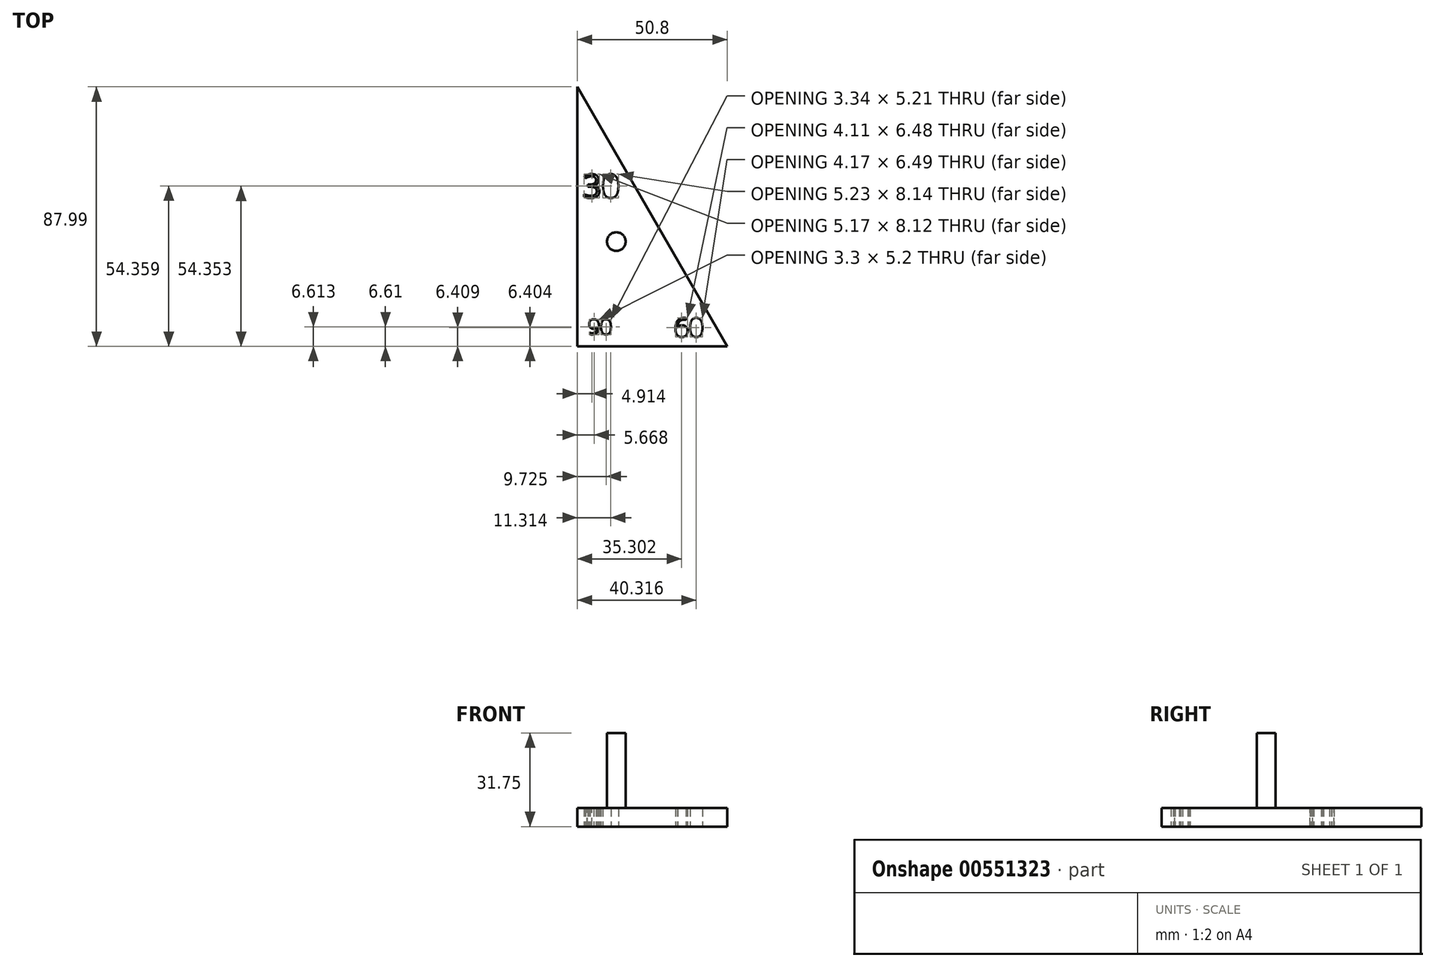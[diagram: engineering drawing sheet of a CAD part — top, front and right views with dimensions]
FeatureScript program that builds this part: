
annotation { "Feature Type Name" : "Feature", "Feature Type Description" : "" }
export const myFeature = defineFeature(function(context is Context, id is Id, definition is map)
    precondition{}
    {
        {
            var Q0;
            Q0=qCreatedBy(makeId("Top.planeOp"),FACE);
            var sketch = newSketch(context, id + "F0", { "sketchPlane" : qUnion([Q0])});
            skLineSegment(sketch, "E0", {"start": v(0, 0) * mm, "end": v(0, 87.99) * mm});
            skLineSegment(sketch, "E1", {"start": v(0, 87.99) * mm, "end": v(50.8, 0) * mm});
            skLineSegment(sketch, "E2", {"start": v(50.8, 0) * mm, "end": v(0, 0) * mm});
            skText(sketch, "E3", { "text": "90", "fontName": "OpenSans-Regular.ttf"});
            skText(sketch, "E4", { "text": "30", "fontName": "OpenSans-Regular.ttf"});
            skText(sketch, "E5", { "text": "60", "fontName": "OpenSans-Regular.ttf"});
            const initialGuessF0  = {"E3": [0.00365, 0.00408, 1, 0, 0.0051], "E4": [0.00182, 0.0504, 1, 0, 0.00797], "E5": [0.03274, 0.00325, 1, 0, 0.00636]};
            skSetInitialGuess(sketch, initialGuessF0);
            skSolve(sketch);
        }
        {
            var Q0;
            Q0 = qSketchRegion(id + "F0", true);
            extrude(context, id + "F1", {"entities" : qUnion([Q0]), "depth" : 6.35 * mm, "offsetDistance" : 25.4 * mm});
        }
        {
            var Q0;
            Q0=makeQuery(id+"F1.opExtrude","CAP_FACE",FACE,{"disambiguationData":[OSD([sQuery(id+"F0.wireOp",EDGE,"E0"),sQuery(id+"F0.wireOp",EDGE,"E1"),sQuery(id+"F0.wireOp",EDGE,"E2"),sQuery(id+"F0.wireOp",EDGE,"E3.sketch_text.stroke-0"),sQuery(id+"F0.wireOp",EDGE,"E3.sketch_text.stroke-1"),sQuery(id+"F0.wireOp",EDGE,"E3.sketch_text.stroke-2"),sQuery(id+"F0.wireOp",EDGE,"E3.sketch_text.stroke-3"),sQuery(id+"F0.wireOp",EDGE,"E3.sketch_text.stroke-4"),sQuery(id+"F0.wireOp",EDGE,"E3.sketch_text.stroke-5"),sQuery(id+"F0.wireOp",EDGE,"E3.sketch_text.stroke-6"),sQuery(id+"F0.wireOp",EDGE,"E3.sketch_text.stroke-7"),sQuery(id+"F0.wireOp",EDGE,"E3.sketch_text.stroke-8"),sQuery(id+"F0.wireOp",EDGE,"E3.sketch_text.stroke-9"),sQuery(id+"F0.wireOp",EDGE,"E3.sketch_text.stroke-10"),sQuery(id+"F0.wireOp",EDGE,"E3.sketch_text.stroke-11"),sQuery(id+"F0.wireOp",EDGE,"E3.sketch_text.stroke-12"),sQuery(id+"F0.wireOp",EDGE,"E3.sketch_text.stroke-13"),sQuery(id+"F0.wireOp",EDGE,"E3.sketch_text.stroke-14"),sQuery(id+"F0.wireOp",EDGE,"E3.sketch_text.stroke-15"),sQuery(id+"F0.wireOp",EDGE,"E3.sketch_text.stroke-26"),sQuery(id+"F0.wireOp",EDGE,"E3.sketch_text.stroke-27"),sQuery(id+"F0.wireOp",EDGE,"E3.sketch_text.stroke-28"),sQuery(id+"F0.wireOp",EDGE,"E3.sketch_text.stroke-29"),sQuery(id+"F0.wireOp",EDGE,"E3.sketch_text.stroke-30"),sQuery(id+"F0.wireOp",EDGE,"E3.sketch_text.stroke-31"),sQuery(id+"F0.wireOp",EDGE,"E3.sketch_text.stroke-32"),sQuery(id+"F0.wireOp",EDGE,"E3.sketch_text.stroke-33"),sQuery(id+"F0.wireOp",EDGE,"E4.sketch_text.stroke-0"),sQuery(id+"F0.wireOp",EDGE,"E4.sketch_text.stroke-1"),sQuery(id+"F0.wireOp",EDGE,"E4.sketch_text.stroke-2"),sQuery(id+"F0.wireOp",EDGE,"E4.sketch_text.stroke-3"),sQuery(id+"F0.wireOp",EDGE,"E4.sketch_text.stroke-4"),sQuery(id+"F0.wireOp",EDGE,"E4.sketch_text.stroke-5"),sQuery(id+"F0.wireOp",EDGE,"E4.sketch_text.stroke-6"),sQuery(id+"F0.wireOp",EDGE,"E4.sketch_text.stroke-7"),sQuery(id+"F0.wireOp",EDGE,"E4.sketch_text.stroke-8"),sQuery(id+"F0.wireOp",EDGE,"E4.sketch_text.stroke-9"),sQuery(id+"F0.wireOp",EDGE,"E4.sketch_text.stroke-10"),sQuery(id+"F0.wireOp",EDGE,"E4.sketch_text.stroke-11"),sQuery(id+"F0.wireOp",EDGE,"E4.sketch_text.stroke-12"),sQuery(id+"F0.wireOp",EDGE,"E4.sketch_text.stroke-13"),sQuery(id+"F0.wireOp",EDGE,"E4.sketch_text.stroke-14"),sQuery(id+"F0.wireOp",EDGE,"E4.sketch_text.stroke-15"),sQuery(id+"F0.wireOp",EDGE,"E4.sketch_text.stroke-16"),sQuery(id+"F0.wireOp",EDGE,"E4.sketch_text.stroke-17"),sQuery(id+"F0.wireOp",EDGE,"E4.sketch_text.stroke-18"),sQuery(id+"F0.wireOp",EDGE,"E4.sketch_text.stroke-19"),sQuery(id+"F0.wireOp",EDGE,"E4.sketch_text.stroke-20"),sQuery(id+"F0.wireOp",EDGE,"E4.sketch_text.stroke-21"),sQuery(id+"F0.wireOp",EDGE,"E4.sketch_text.stroke-22"),sQuery(id+"F0.wireOp",EDGE,"E4.sketch_text.stroke-23"),sQuery(id+"F0.wireOp",EDGE,"E4.sketch_text.stroke-24"),sQuery(id+"F0.wireOp",EDGE,"E4.sketch_text.stroke-25"),sQuery(id+"F0.wireOp",EDGE,"E4.sketch_text.stroke-26"),sQuery(id+"F0.wireOp",EDGE,"E4.sketch_text.stroke-27"),sQuery(id+"F0.wireOp",EDGE,"E4.sketch_text.stroke-28"),sQuery(id+"F0.wireOp",EDGE,"E4.sketch_text.stroke-29"),sQuery(id+"F0.wireOp",EDGE,"E4.sketch_text.stroke-30"),sQuery(id+"F0.wireOp",EDGE,"E4.sketch_text.stroke-31"),sQuery(id+"F0.wireOp",EDGE,"E4.sketch_text.stroke-32"),sQuery(id+"F0.wireOp",EDGE,"E4.sketch_text.stroke-33"),sQuery(id+"F0.wireOp",EDGE,"E4.sketch_text.stroke-34"),sQuery(id+"F0.wireOp",EDGE,"E4.sketch_text.stroke-35"),sQuery(id+"F0.wireOp",EDGE,"E5.sketch_text.stroke-0"),sQuery(id+"F0.wireOp",EDGE,"E5.sketch_text.stroke-1"),sQuery(id+"F0.wireOp",EDGE,"E5.sketch_text.stroke-2"),sQuery(id+"F0.wireOp",EDGE,"E5.sketch_text.stroke-3"),sQuery(id+"F0.wireOp",EDGE,"E5.sketch_text.stroke-4"),sQuery(id+"F0.wireOp",EDGE,"E5.sketch_text.stroke-5"),sQuery(id+"F0.wireOp",EDGE,"E5.sketch_text.stroke-6"),sQuery(id+"F0.wireOp",EDGE,"E5.sketch_text.stroke-7"),sQuery(id+"F0.wireOp",EDGE,"E5.sketch_text.stroke-8"),sQuery(id+"F0.wireOp",EDGE,"E5.sketch_text.stroke-9"),sQuery(id+"F0.wireOp",EDGE,"E5.sketch_text.stroke-10"),sQuery(id+"F0.wireOp",EDGE,"E5.sketch_text.stroke-11"),sQuery(id+"F0.wireOp",EDGE,"E5.sketch_text.stroke-12"),sQuery(id+"F0.wireOp",EDGE,"E5.sketch_text.stroke-13"),sQuery(id+"F0.wireOp",EDGE,"E5.sketch_text.stroke-14"),sQuery(id+"F0.wireOp",EDGE,"E5.sketch_text.stroke-25"),sQuery(id+"F0.wireOp",EDGE,"E5.sketch_text.stroke-26"),sQuery(id+"F0.wireOp",EDGE,"E5.sketch_text.stroke-27"),sQuery(id+"F0.wireOp",EDGE,"E5.sketch_text.stroke-28"),sQuery(id+"F0.wireOp",EDGE,"E5.sketch_text.stroke-29"),sQuery(id+"F0.wireOp",EDGE,"E5.sketch_text.stroke-30"),sQuery(id+"F0.wireOp",EDGE,"E5.sketch_text.stroke-31"),sQuery(id+"F0.wireOp",EDGE,"E5.sketch_text.stroke-32")])],"isStart":false});
            var sketch = newSketch(context, id + "F2", { "sketchPlane" : qUnion([Q0])});
            skCircle(sketch, "E6", {"center": v(13.22, 35.52) * mm, "radius": 3.18 * mm});
            skSolve(sketch);
        }
        {
            var Q0;
            Q0=makeQuery(id+"F2.imprint","IMPRINT",FACE,{"disambiguationData":[TD([[makeQuery(id+"F2.imprint","IMPRINT",EDGE,{"derivedFrom":sQuery(id+"F2.wireOp",EDGE,"E6")}),1.0]])]});
            extrude(context, id + "F3", {"entities" : qUnion([Q0]), "operationType" : NewBodyOperationType.ADD, "depth" : 25.4 * mm, "offsetDistance" : 25.4 * mm});
        }
    });
